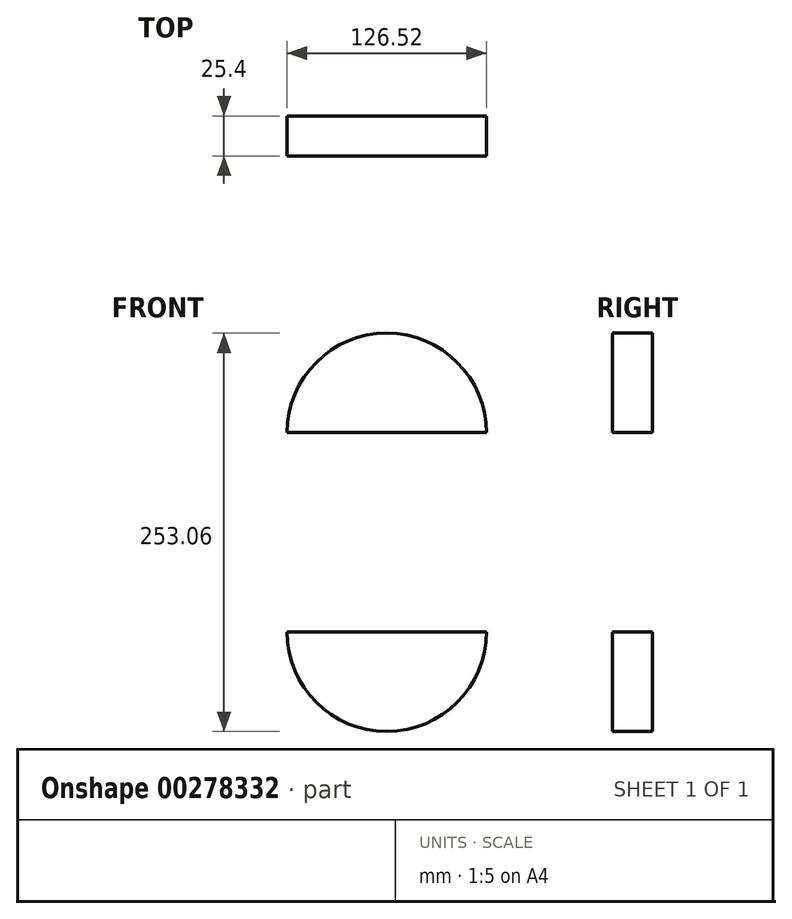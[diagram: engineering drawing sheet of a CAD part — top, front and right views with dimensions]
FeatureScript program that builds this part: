
annotation { "Feature Type Name" : "Feature", "Feature Type Description" : "" }
export const myFeature = defineFeature(function(context is Context, id is Id, definition is map)
    precondition{}
    {
        {
            var Q0;
            Q0=qCreatedBy(makeId("Front.planeOp"),FACE);
            var sketch = newSketch(context, id + "F0", { "sketchPlane" : qUnion([Q0])});
            skCircle(sketch, "E0", {"center": v(0, 0) * mm, "radius": 63.26 * mm});
            skLineSegment(sketch, "E1", {"start": v(0, 63.26) * mm, "end": v(0, -63.26) * mm});
            skCircle(sketch, "E2", {"center": v(0, -63.26) * mm, "radius": 63.26 * mm});
            skCircle(sketch, "E3", {"center": v(0, 63.26) * mm, "radius": 63.26 * mm});
            skLineSegment(sketch, "E4", {"start": v(0, 63.26) * mm, "end": v(63.26, 63.26) * mm});
            skLineSegment(sketch, "E5", {"start": v(0, 63.26) * mm, "end": v(-63.26, 63.26) * mm});
            skLineSegment(sketch, "E6", {"start": v(0, -63.26) * mm, "end": v(-63.26, -63.26) * mm});
            skLineSegment(sketch, "E7", {"start": v(0, -63.26) * mm, "end": v(63.26, -63.26) * mm});
            skSolve(sketch);
        }
        {
            var Q0;
            {var subQ0=sQuery(id+"F0.wireOp",EDGE,"E4");Q0=makeQuery(id+"F0.imprint","IMPRINT",FACE,{"disambiguationData":[TD([[makeQuery(id+"F0.imprint","IMPRINT",EDGE,{"derivedFrom":subQ0}),1.0]])]});}
            extrude(context, id + "F1", {"entities" : qUnion([Q0]), "depth" : 25.4 * mm});
        }
        {
            var Q0;
            {var subQ0=sQuery(id+"F0.wireOp",EDGE,"E6");Q0=makeQuery(id+"F0.imprint","IMPRINT",FACE,{"disambiguationData":[TD([[makeQuery(id+"F0.imprint","IMPRINT",EDGE,{"derivedFrom":subQ0}),1.0]])]});}
            extrude(context, id + "F2", {"entities" : qUnion([Q0]), "depth" : 25.4 * mm});
        }
    });
